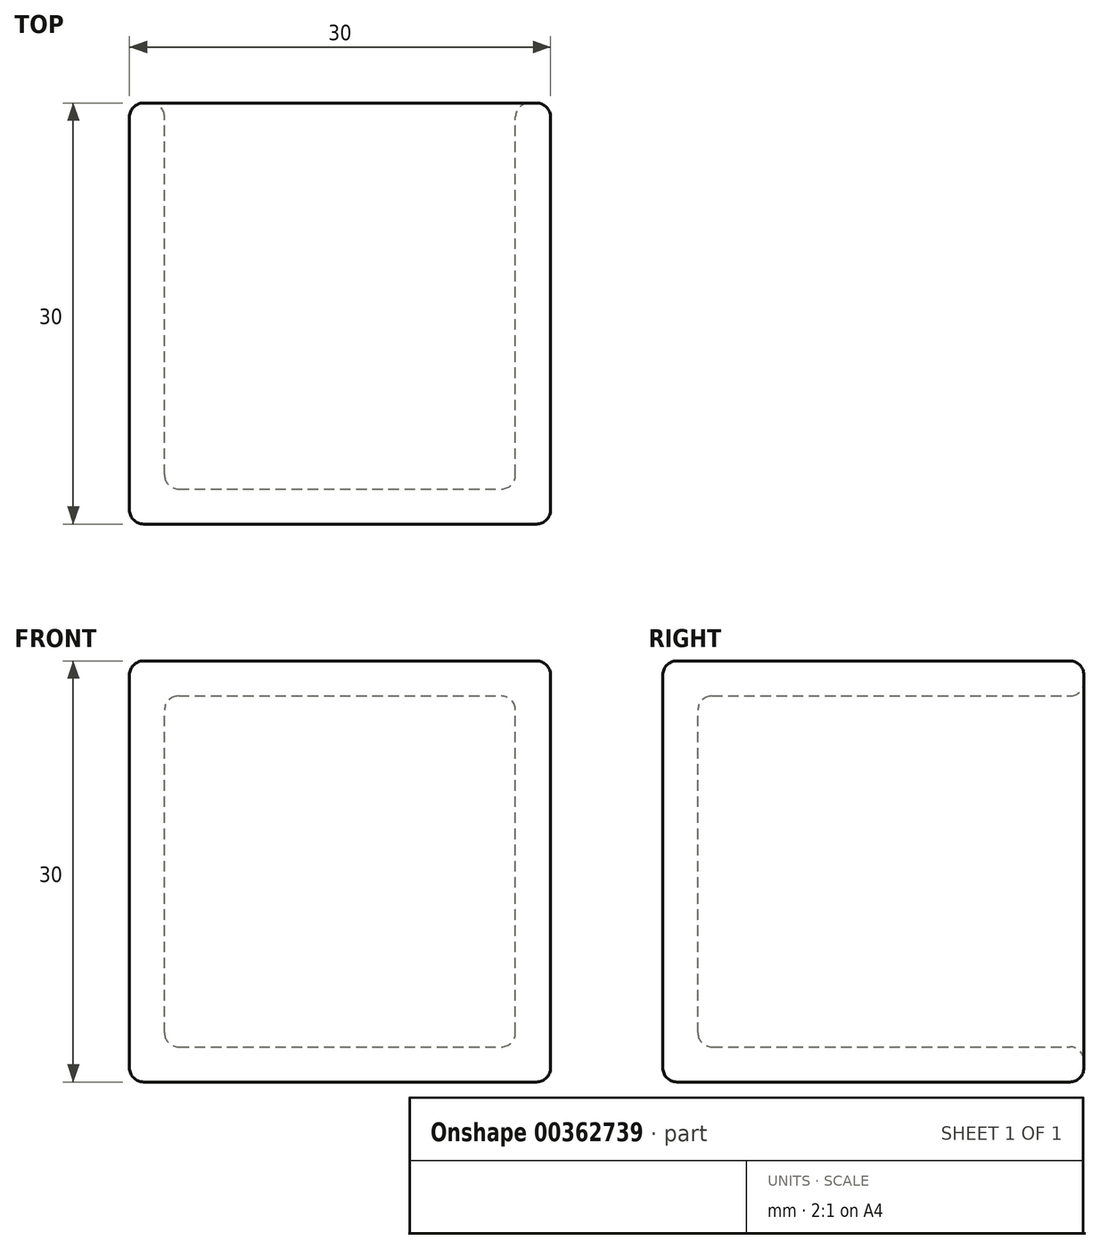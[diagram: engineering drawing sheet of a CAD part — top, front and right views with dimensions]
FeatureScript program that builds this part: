
annotation { "Feature Type Name" : "Feature", "Feature Type Description" : "" }
export const myFeature = defineFeature(function(context is Context, id is Id, definition is map)
    precondition{}
    {
        {
            var Q0;
            Q0=qCreatedBy(makeId("Front.planeOp"),FACE);
            var sketch = newSketch(context, id + "F0", { "sketchPlane" : qUnion([Q0])});
            skLineSegment(sketch, "E0.bottom", {"start": v(0, 0) * mm, "end": v(30, 0) * mm});
            skLineSegment(sketch, "E0.top", {"start": v(0, 30) * mm, "end": v(30, 30) * mm});
            skLineSegment(sketch, "E0.left", {"start": v(0, 0) * mm, "end": v(0, 30) * mm});
            skLineSegment(sketch, "E0.right", {"start": v(30, 0) * mm, "end": v(30, 30) * mm});
            skSolve(sketch);
        }
        {
            var Q0;
            Q0 = qSketchRegion(id + "F0", true);
            extrude(context, id + "F1", {"entities" : qUnion([Q0]), "depth" : 30 * mm});
        }
        {
            var Q0;
            Q0=makeQuery(id+"F1.opExtrude","CAP_FACE",FACE,{"disambiguationData":[OSD([sQuery(id+"F0.wireOp",EDGE,"E0.bottom"),sQuery(id+"F0.wireOp",EDGE,"E0.top"),sQuery(id+"F0.wireOp",EDGE,"E0.left"),sQuery(id+"F0.wireOp",EDGE,"E0.right")])],"isStart":true});
            shell(context, id + "F2", {"entities" : qUnion([Q0]), "thickness" : 2.5 * mm});
        }
        {
            var Q0;
            Q0=makeQuery(id+"F1.opExtrude","SWEPT_EDGE",EDGE,{"disambiguationData":[OSD([sQuery(id+"F0.wireOp",EDGE,"E0.top"),sQuery(id+"F0.wireOp",EDGE,"E0.right")])]});
            var Q1;
            Q1=makeQuery(id+"F1.opExtrude","SWEPT_EDGE",EDGE,{"disambiguationData":[OSD([sQuery(id+"F0.wireOp",EDGE,"E0.top"),sQuery(id+"F0.wireOp",EDGE,"E0.left")])]});
            var Q2;
            Q2=makeQuery(id+"F1.opExtrude","SWEPT_EDGE",EDGE,{"disambiguationData":[OSD([sQuery(id+"F0.wireOp",EDGE,"E0.bottom"),sQuery(id+"F0.wireOp",EDGE,"E0.right")])]});
            var Q3;
            Q3=makeQuery(id+"F2.opShell","OFFSET_EDGE",EDGE,{"disambiguationData":[OSD([sQuery(id+"F0.wireOp",EDGE,"E0.bottom"),sQuery(id+"F0.wireOp",EDGE,"E0.left")])]});
            var Q4;
            Q4=makeQuery(id+"F1.opExtrude","CAP_EDGE",EDGE,{"disambiguationData":[OSD([sQuery(id+"F0.wireOp",EDGE,"E0.left")])],"isStart":true});
            var Q5;
            Q5=makeQuery(id+"F1.opExtrude","CAP_EDGE",EDGE,{"disambiguationData":[OSD([sQuery(id+"F0.wireOp",EDGE,"E0.bottom")])],"isStart":true});
            var Q6;
            Q6=makeQuery(id+"F1.opExtrude","CAP_EDGE",EDGE,{"disambiguationData":[OSD([sQuery(id+"F0.wireOp",EDGE,"E0.bottom")])],"isStart":false});
            var Q7;
            Q7=makeQuery(id+"F1.opExtrude","CAP_EDGE",EDGE,{"disambiguationData":[OSD([sQuery(id+"F0.wireOp",EDGE,"E0.top")])],"isStart":true});
            var Q8;
            Q8=makeQuery(id+"F1.opExtrude","CAP_EDGE",EDGE,{"disambiguationData":[OSD([sQuery(id+"F0.wireOp",EDGE,"E0.top")])],"isStart":false});
            var Q9;
            Q9=makeQuery(id+"F1.opExtrude","CAP_EDGE",EDGE,{"disambiguationData":[OSD([sQuery(id+"F0.wireOp",EDGE,"E0.left")])],"isStart":false});
            var Q10;
            Q10=makeQuery(id+"F1.opExtrude","CAP_EDGE",EDGE,{"disambiguationData":[OSD([sQuery(id+"F0.wireOp",EDGE,"E0.right")])],"isStart":true});
            var Q11;
            Q11=makeQuery(id+"F1.opExtrude","CAP_EDGE",EDGE,{"disambiguationData":[OSD([sQuery(id+"F0.wireOp",EDGE,"E0.right")])],"isStart":false});
            var Q12;
            Q12=makeQuery(id+"F2.opShell","OFFSET_EDGE",EDGE,{"disambiguationData":[OSD([sQuery(id+"F0.wireOp",EDGE,"E0.bottom"),sQuery(id+"F0.wireOp",EDGE,"E0.right")])]});
            var Q13;
            Q13=makeQuery(id+"F2.opShell","OFFSET_EDGE",EDGE,{"disambiguationData":[OSD([sQuery(id+"F0.wireOp",EDGE,"E0.top"),sQuery(id+"F0.wireOp",EDGE,"E0.left")])]});
            var Q14;
            Q14=makeQuery(id+"F2.opShell","OFFSET_EDGE",EDGE,{"disambiguationData":[OSD([sQuery(id+"F0.wireOp",EDGE,"E0.top"),sQuery(id+"F0.wireOp",EDGE,"E0.right")])]});
            var Q15;
            {var subQ0=sQuery(id+"F0.wireOp",EDGE,"E0.bottom");Q15=makeQuery(id+"F2.opShell","OFFSET_EDGE",EDGE,{"disambiguationData":[OSD([subQ0]),TDD([makeQuery(id+"F1.opExtrude","CAP_EDGE",EDGE,{"disambiguationData":[OSD([subQ0])],"isStart":true})])]});}
            var Q16;
            {var subQ0=sQuery(id+"F0.wireOp",EDGE,"E0.bottom");Q16=makeQuery(id+"F2.opShell","OFFSET_EDGE",EDGE,{"disambiguationData":[OSD([subQ0]),TDD([makeQuery(id+"F1.opExtrude","CAP_EDGE",EDGE,{"disambiguationData":[OSD([subQ0])],"isStart":false})])]});}
            var Q17;
            {var subQ0=sQuery(id+"F0.wireOp",EDGE,"E0.top");Q17=makeQuery(id+"F2.opShell","OFFSET_EDGE",EDGE,{"disambiguationData":[OSD([subQ0]),TDD([makeQuery(id+"F1.opExtrude","CAP_EDGE",EDGE,{"disambiguationData":[OSD([subQ0])],"isStart":true})])]});}
            var Q18;
            {var subQ0=sQuery(id+"F0.wireOp",EDGE,"E0.top");Q18=makeQuery(id+"F2.opShell","OFFSET_EDGE",EDGE,{"disambiguationData":[OSD([subQ0]),TDD([makeQuery(id+"F1.opExtrude","CAP_EDGE",EDGE,{"disambiguationData":[OSD([subQ0])],"isStart":false})])]});}
            var Q19;
            {var subQ0=sQuery(id+"F0.wireOp",EDGE,"E0.left");Q19=makeQuery(id+"F2.opShell","OFFSET_EDGE",EDGE,{"disambiguationData":[OSD([subQ0]),TDD([makeQuery(id+"F1.opExtrude","CAP_EDGE",EDGE,{"disambiguationData":[OSD([subQ0])],"isStart":true})])]});}
            var Q20;
            {var subQ0=sQuery(id+"F0.wireOp",EDGE,"E0.left");Q20=makeQuery(id+"F2.opShell","OFFSET_EDGE",EDGE,{"disambiguationData":[OSD([subQ0]),TDD([makeQuery(id+"F1.opExtrude","CAP_EDGE",EDGE,{"disambiguationData":[OSD([subQ0])],"isStart":false})])]});}
            var Q21;
            {var subQ0=sQuery(id+"F0.wireOp",EDGE,"E0.right");Q21=makeQuery(id+"F2.opShell","OFFSET_EDGE",EDGE,{"disambiguationData":[OSD([subQ0]),TDD([makeQuery(id+"F1.opExtrude","CAP_EDGE",EDGE,{"disambiguationData":[OSD([subQ0])],"isStart":true})])]});}
            var Q22;
            {var subQ0=sQuery(id+"F0.wireOp",EDGE,"E0.right");Q22=makeQuery(id+"F2.opShell","OFFSET_EDGE",EDGE,{"disambiguationData":[OSD([subQ0]),TDD([makeQuery(id+"F1.opExtrude","CAP_EDGE",EDGE,{"disambiguationData":[OSD([subQ0])],"isStart":false})])]});}
            var Q23;
            Q23=makeQuery(id+"F1.opExtrude","SWEPT_EDGE",EDGE,{"disambiguationData":[OSD([sQuery(id+"F0.wireOp",EDGE,"E0.bottom"),sQuery(id+"F0.wireOp",EDGE,"E0.left")])]});
            fillet(context, id + "F3", {"entities" : qUnion([Q0, Q1, Q2, Q3, Q4, Q5, Q6, Q7, Q8, Q9, Q10, Q11, Q12, Q13, Q14, Q15, Q16, Q17, Q18, Q19, Q20, Q21, Q22, Q23]), "radius" : 1 * mm, "tangentPropagation" : true, "allowEdgeOverflow" : false});
        }
    });
